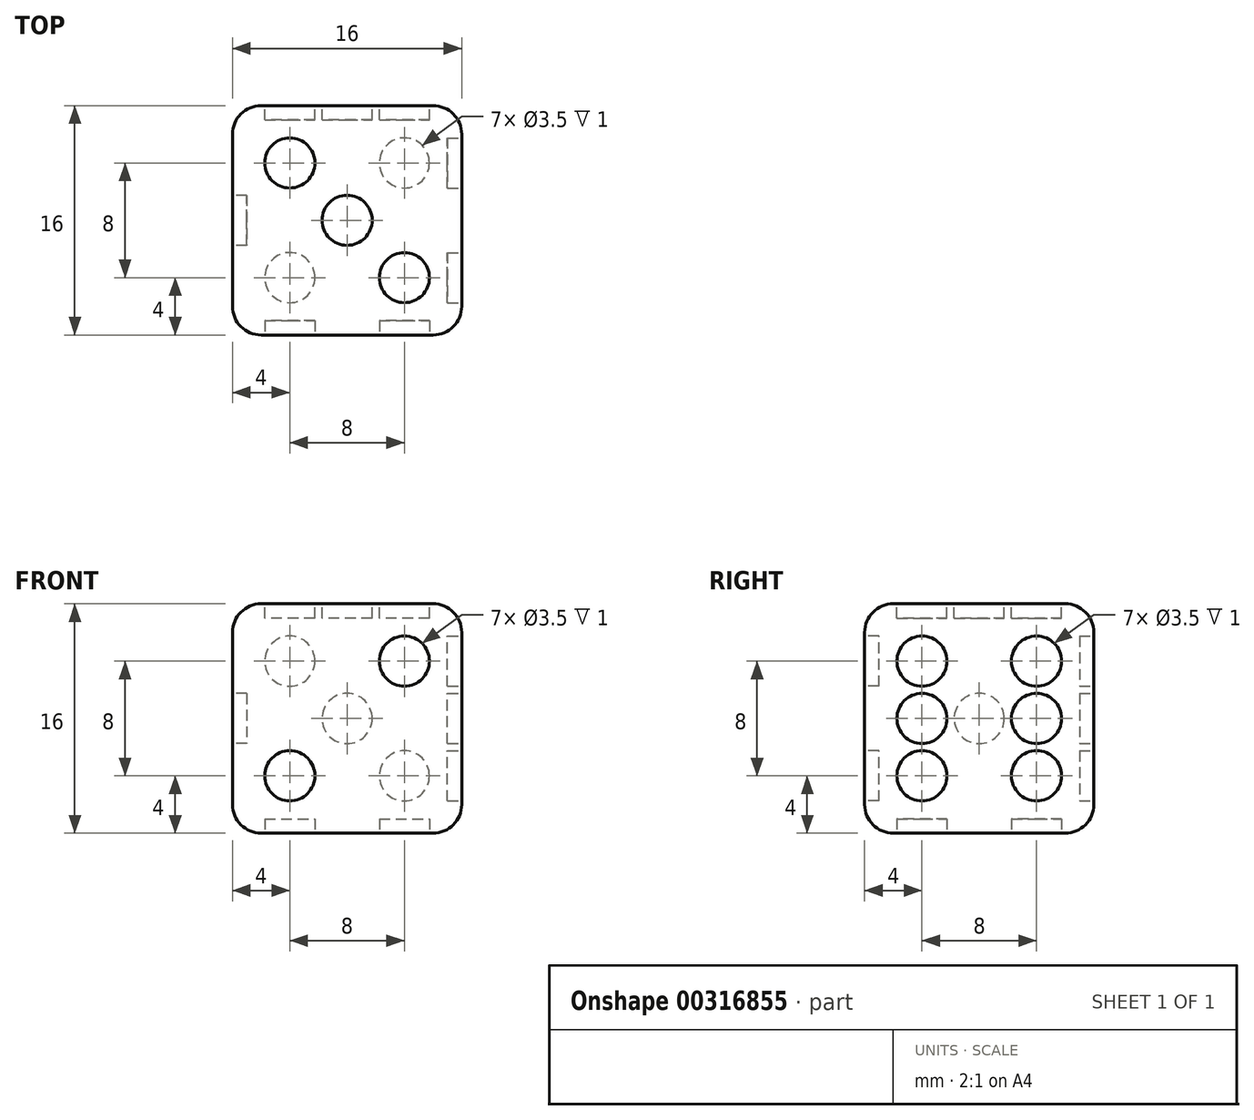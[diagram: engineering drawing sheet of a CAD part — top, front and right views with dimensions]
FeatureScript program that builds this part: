
annotation { "Feature Type Name" : "Feature", "Feature Type Description" : "" }
export const myFeature = defineFeature(function(context is Context, id is Id, definition is map)
    precondition{}
    {
        {
            var Q0;
            Q0=qCreatedBy(makeId("Top.planeOp"),FACE);
            var sketch = newSketch(context, id + "F0", { "sketchPlane" : qUnion([Q0])});
            skLineSegment(sketch, "E0.bottom", {"start": v(8, -8) * mm, "end": v(-8, -8) * mm});
            skLineSegment(sketch, "E0.top", {"start": v(8, 8) * mm, "end": v(-8, 8) * mm});
            skLineSegment(sketch, "E0.left", {"start": v(8, -8) * mm, "end": v(8, 8) * mm});
            skLineSegment(sketch, "E0.right", {"start": v(-8, -8) * mm, "end": v(-8, 8) * mm});
            skPoint(sketch, "E0.middle", {"position": v(0, 0) * mm});
            skSolve(sketch);
        }
        {
            var Q0;
            Q0=makeQuery(id+"F0.imprint","IMPRINT",FACE,{"disambiguationData":[TD([[makeQuery(id+"F0.imprint","IMPRINT",EDGE,{"derivedFrom":sQuery(id+"F0.wireOp",EDGE,"E0.bottom")}),-1.0]])]});
            extrude(context, id + "F1", {"entities" : qUnion([Q0]), "depth" : 16 * mm});
        }
        {
            var Q0;
            Q0=makeQuery(id+"F1.opExtrude","SWEPT_FACE",FACE,{"disambiguationData":[OSD([sQuery(id+"F0.wireOp",EDGE,"E0.top")])]});
            var sketch = newSketch(context, id + "F2", { "sketchPlane" : qUnion([Q0])});
            skCircle(sketch, "E1", {"center": v(-4, 4) * mm, "radius": 1.75 * mm});
            skCircle(sketch, "E2", {"center": v(4, 12) * mm, "radius": 1.75 * mm});
            skCircle(sketch, "E3", {"center": v(-4, 12) * mm, "radius": 1.75 * mm});
            skCircle(sketch, "E4", {"center": v(4, 4) * mm, "radius": 1.75 * mm});
            skCircle(sketch, "E5", {"center": v(0, 8) * mm, "radius": 1.75 * mm});
            skSolve(sketch);
        }
        {
            var Q0;
            Q0=makeQuery(id+"F2.imprint","IMPRINT",FACE,{"disambiguationData":[TD([[makeQuery(id+"F2.imprint","IMPRINT",EDGE,{"derivedFrom":sQuery(id+"F2.wireOp",EDGE,"E2")}),1.0]])]});
            var Q1;
            Q1=makeQuery(id+"F2.imprint","IMPRINT",FACE,{"disambiguationData":[TD([[makeQuery(id+"F2.imprint","IMPRINT",EDGE,{"derivedFrom":sQuery(id+"F2.wireOp",EDGE,"E1")}),1.0]])]});
            extrude(context, id + "F3", {"entities" : qUnion([Q0, Q1]), "operationType" : NewBodyOperationType.REMOVE, "oppositeDirection" : true, "depth" : 1 * mm});
        }
        {
            var Q0;
            Q0=makeQuery(id+"F2.imprint","IMPRINT",FACE,{"disambiguationData":[TD([[makeQuery(id+"F2.imprint","IMPRINT",EDGE,{"derivedFrom":sQuery(id+"F2.wireOp",EDGE,"E3")}),1.0]])]});
            var Q1;
            Q1=makeQuery(id+"F2.imprint","IMPRINT",FACE,{"disambiguationData":[TD([[makeQuery(id+"F2.imprint","IMPRINT",EDGE,{"derivedFrom":sQuery(id+"F2.wireOp",EDGE,"E5")}),1.0]])]});
            var Q2;
            Q2=makeQuery(id+"F2.imprint","IMPRINT",FACE,{"disambiguationData":[TD([[makeQuery(id+"F2.imprint","IMPRINT",EDGE,{"derivedFrom":sQuery(id+"F2.wireOp",EDGE,"E4")}),1.0]])]});
            extrude(context, id + "F4", {"entities" : qUnion([Q0, Q1, Q2]), "operationType" : NewBodyOperationType.REMOVE, "oppositeDirection" : true, "depth" : 1 * mm});
        }
        {
            var Q0;
            Q0=makeQuery(id+"F1.opExtrude","SWEPT_FACE",FACE,{"disambiguationData":[OSD([sQuery(id+"F0.wireOp",EDGE,"E0.bottom")])]});
            var sketch = newSketch(context, id + "F5", { "sketchPlane" : qUnion([Q0])});
            skCircle(sketch, "E6", {"center": v(-4, 4) * mm, "radius": 1.75 * mm});
            skCircle(sketch, "E7", {"center": v(4, 12) * mm, "radius": 1.75 * mm});
            skSolve(sketch);
        }
        {
            var Q0;
            Q0=makeQuery(id+"F5.imprint","IMPRINT",FACE,{"disambiguationData":[TD([[makeQuery(id+"F5.imprint","IMPRINT",EDGE,{"derivedFrom":sQuery(id+"F5.wireOp",EDGE,"E6")}),1.0]])]});
            var Q1;
            Q1=makeQuery(id+"F5.imprint","IMPRINT",FACE,{"disambiguationData":[TD([[makeQuery(id+"F5.imprint","IMPRINT",EDGE,{"derivedFrom":sQuery(id+"F5.wireOp",EDGE,"E7")}),1.0]])]});
            extrude(context, id + "F6", {"entities" : qUnion([Q0, Q1]), "operationType" : NewBodyOperationType.REMOVE, "oppositeDirection" : true, "depth" : 1 * mm});
        }
        {
            var Q0;
            Q0=makeQuery(id+"F1.opExtrude","CAP_FACE",FACE,{"disambiguationData":[OSD([sQuery(id+"F0.wireOp",EDGE,"E0.bottom"),sQuery(id+"F0.wireOp",EDGE,"E0.top"),sQuery(id+"F0.wireOp",EDGE,"E0.left"),sQuery(id+"F0.wireOp",EDGE,"E0.right")])],"isStart":false});
            var sketch = newSketch(context, id + "F7", { "sketchPlane" : qUnion([Q0])});
            skCircle(sketch, "E8", {"center": v(0, 0) * mm, "radius": 1.75 * mm});
            skCircle(sketch, "E9", {"center": v(4, -4) * mm, "radius": 1.75 * mm});
            skCircle(sketch, "E10", {"center": v(-4, 4) * mm, "radius": 1.75 * mm});
            skSolve(sketch);
        }
        {
            var Q0;
            Q0=makeQuery(id+"F7.imprint","IMPRINT",FACE,{"disambiguationData":[TD([[makeQuery(id+"F7.imprint","IMPRINT",EDGE,{"derivedFrom":sQuery(id+"F7.wireOp",EDGE,"h1jGjn2j-waux-BRHr-8ZsS-qUSvsllOvU67")}),1.0]])]});
            var Q1;
            Q1=makeQuery(id+"F7.imprint","IMPRINT",FACE,{"disambiguationData":[TD([[makeQuery(id+"F7.imprint","IMPRINT",EDGE,{"derivedFrom":sQuery(id+"F7.wireOp",EDGE,"E8")}),1.0]])]});
            var Q2;
            Q2=makeQuery(id+"F7.imprint","IMPRINT",FACE,{"disambiguationData":[TD([[makeQuery(id+"F7.imprint","IMPRINT",EDGE,{"derivedFrom":sQuery(id+"F7.wireOp",EDGE,"c6qNiyI0-zUlM-MVL6-RI8d-L9UIt0NrfZDj")}),1.0]])]});
            var Q3;
            Q3=makeQuery(id+"F7.imprint","IMPRINT",FACE,{"disambiguationData":[TD([[makeQuery(id+"F7.imprint","IMPRINT",EDGE,{"derivedFrom":sQuery(id+"F7.wireOp",EDGE,"E9")}),1.0]])]});
            var Q4;
            Q4=makeQuery(id+"F7.imprint","IMPRINT",FACE,{"disambiguationData":[TD([[makeQuery(id+"F7.imprint","IMPRINT",EDGE,{"derivedFrom":sQuery(id+"F7.wireOp",EDGE,"E10")}),1.0]])]});
            extrude(context, id + "F8", {"entities" : qUnion([Q0, Q1, Q2, Q3, Q4]), "operationType" : NewBodyOperationType.REMOVE, "oppositeDirection" : true, "depth" : 1 * mm});
        }
        {
            var Q0;
            Q0=makeQuery(id+"F1.opExtrude","SWEPT_FACE",FACE,{"disambiguationData":[OSD([sQuery(id+"F0.wireOp",EDGE,"E0.left")])]});
            var sketch = newSketch(context, id + "F9", { "sketchPlane" : qUnion([Q0])});
            skCircle(sketch, "E11", {"center": v(-4, 12) * mm, "radius": 1.75 * mm});
            skCircle(sketch, "E12", {"center": v(-4, 8) * mm, "radius": 1.75 * mm});
            skCircle(sketch, "E13", {"center": v(-4, 4) * mm, "radius": 1.75 * mm});
            skCircle(sketch, "E14", {"center": v(4, 4) * mm, "radius": 1.75 * mm});
            skCircle(sketch, "E15", {"center": v(4, 8) * mm, "radius": 1.75 * mm});
            skCircle(sketch, "E16", {"center": v(4, 12) * mm, "radius": 1.75 * mm});
            skSolve(sketch);
        }
        {
            var Q0;
            Q0=makeQuery(id+"F9.imprint","IMPRINT",FACE,{"disambiguationData":[TD([[makeQuery(id+"F9.imprint","IMPRINT",EDGE,{"derivedFrom":sQuery(id+"F9.wireOp",EDGE,"E11")}),1.0]])]});
            var Q1;
            Q1=makeQuery(id+"F9.imprint","IMPRINT",FACE,{"disambiguationData":[TD([[makeQuery(id+"F9.imprint","IMPRINT",EDGE,{"derivedFrom":sQuery(id+"F9.wireOp",EDGE,"E13")}),1.0]])]});
            var Q2;
            Q2=makeQuery(id+"F9.imprint","IMPRINT",FACE,{"disambiguationData":[TD([[makeQuery(id+"F9.imprint","IMPRINT",EDGE,{"derivedFrom":sQuery(id+"F9.wireOp",EDGE,"E14")}),1.0]])]});
            var Q3;
            Q3=makeQuery(id+"F9.imprint","IMPRINT",FACE,{"disambiguationData":[TD([[makeQuery(id+"F9.imprint","IMPRINT",EDGE,{"derivedFrom":sQuery(id+"F9.wireOp",EDGE,"E15")}),1.0]])]});
            var Q4;
            Q4=makeQuery(id+"F9.imprint","IMPRINT",FACE,{"disambiguationData":[TD([[makeQuery(id+"F9.imprint","IMPRINT",EDGE,{"derivedFrom":sQuery(id+"F9.wireOp",EDGE,"E16")}),1.0]])]});
            var Q5;
            Q5=makeQuery(id+"F9.imprint","IMPRINT",FACE,{"disambiguationData":[TD([[makeQuery(id+"F9.imprint","IMPRINT",EDGE,{"derivedFrom":sQuery(id+"F9.wireOp",EDGE,"E12")}),1.0]])]});
            extrude(context, id + "F10", {"entities" : qUnion([Q0, Q1, Q2, Q3, Q4, Q5]), "operationType" : NewBodyOperationType.REMOVE, "oppositeDirection" : true, "depth" : 1 * mm});
        }
        {
            var Q0;
            Q0=makeQuery(id+"F1.opExtrude","CAP_FACE",FACE,{"disambiguationData":[OSD([sQuery(id+"F0.wireOp",EDGE,"E0.bottom"),sQuery(id+"F0.wireOp",EDGE,"E0.top"),sQuery(id+"F0.wireOp",EDGE,"E0.left"),sQuery(id+"F0.wireOp",EDGE,"E0.right")])],"isStart":true});
            var sketch = newSketch(context, id + "F11", { "sketchPlane" : qUnion([Q0])});
            skCircle(sketch, "E17", {"center": v(4, -4) * mm, "radius": 1.75 * mm});
            skCircle(sketch, "E18", {"center": v(-4, -4) * mm, "radius": 1.75 * mm});
            skCircle(sketch, "E19", {"center": v(-4, 4) * mm, "radius": 1.75 * mm});
            skCircle(sketch, "E20", {"center": v(4, 4) * mm, "radius": 1.75 * mm});
            skSolve(sketch);
        }
        {
            var Q0;
            Q0=makeQuery(id+"F11.imprint","IMPRINT",FACE,{"disambiguationData":[TD([[makeQuery(id+"F11.imprint","IMPRINT",EDGE,{"derivedFrom":sQuery(id+"F11.wireOp",EDGE,"E17")}),1.0]])]});
            var Q1;
            Q1=makeQuery(id+"F11.imprint","IMPRINT",FACE,{"disambiguationData":[TD([[makeQuery(id+"F11.imprint","IMPRINT",EDGE,{"derivedFrom":sQuery(id+"F11.wireOp",EDGE,"E19")}),1.0]])]});
            var Q2;
            Q2=makeQuery(id+"F11.imprint","IMPRINT",FACE,{"disambiguationData":[TD([[makeQuery(id+"F11.imprint","IMPRINT",EDGE,{"derivedFrom":sQuery(id+"F11.wireOp",EDGE,"E20")}),1.0]])]});
            var Q3;
            Q3=makeQuery(id+"F11.imprint","IMPRINT",FACE,{"disambiguationData":[TD([[makeQuery(id+"F11.imprint","IMPRINT",EDGE,{"derivedFrom":sQuery(id+"F11.wireOp",EDGE,"E18")}),1.0]])]});
            extrude(context, id + "F12", {"entities" : qUnion([Q0, Q1, Q2, Q3]), "operationType" : NewBodyOperationType.REMOVE, "oppositeDirection" : true, "depth" : 1 * mm});
        }
        {
            var Q0;
            Q0=makeQuery(id+"F1.opExtrude","SWEPT_FACE",FACE,{"disambiguationData":[OSD([sQuery(id+"F0.wireOp",EDGE,"E0.right")])]});
            var sketch = newSketch(context, id + "F13", { "sketchPlane" : qUnion([Q0])});
            skCircle(sketch, "E21", {"center": v(0, 8) * mm, "radius": 1.75 * mm});
            skSolve(sketch);
        }
        {
            var Q0;
            Q0=makeQuery(id+"F13.imprint","IMPRINT",FACE,{"disambiguationData":[TD([[makeQuery(id+"F13.imprint","IMPRINT",EDGE,{"derivedFrom":sQuery(id+"F13.wireOp",EDGE,"E21")}),1.0]])]});
            extrude(context, id + "F14", {"entities" : qUnion([Q0]), "operationType" : NewBodyOperationType.REMOVE, "oppositeDirection" : true, "depth" : 1 * mm});
        }
        {
            var Q0;
            Q0=makeQuery(id+"F1.opExtrude","CAP_EDGE",EDGE,{"disambiguationData":[OSD([sQuery(id+"F0.wireOp",EDGE,"E0.left")])],"isStart":false});
            var Q1;
            Q1=makeQuery(id+"F1.opExtrude","CAP_EDGE",EDGE,{"disambiguationData":[OSD([sQuery(id+"F0.wireOp",EDGE,"E0.top")])],"isStart":false});
            var Q2;
            Q2=makeQuery(id+"F1.opExtrude","CAP_EDGE",EDGE,{"disambiguationData":[OSD([sQuery(id+"F0.wireOp",EDGE,"E0.right")])],"isStart":false});
            var Q3;
            Q3=makeQuery(id+"F1.opExtrude","CAP_EDGE",EDGE,{"disambiguationData":[OSD([sQuery(id+"F0.wireOp",EDGE,"E0.bottom")])],"isStart":false});
            var Q4;
            Q4=makeQuery(id+"F1.opExtrude","SWEPT_EDGE",EDGE,{"disambiguationData":[OSD([sQuery(id+"F0.wireOp",EDGE,"E0.bottom"),sQuery(id+"F0.wireOp",EDGE,"E0.right")])]});
            var Q5;
            Q5=makeQuery(id+"F1.opExtrude","SWEPT_EDGE",EDGE,{"disambiguationData":[OSD([sQuery(id+"F0.wireOp",EDGE,"E0.top"),sQuery(id+"F0.wireOp",EDGE,"E0.right")])]});
            var Q6;
            Q6=makeQuery(id+"F1.opExtrude","CAP_EDGE",EDGE,{"disambiguationData":[OSD([sQuery(id+"F0.wireOp",EDGE,"E0.right")])],"isStart":true});
            var Q7;
            Q7=makeQuery(id+"F1.opExtrude","CAP_EDGE",EDGE,{"disambiguationData":[OSD([sQuery(id+"F0.wireOp",EDGE,"E0.bottom")])],"isStart":true});
            var Q8;
            Q8=makeQuery(id+"F1.opExtrude","SWEPT_EDGE",EDGE,{"disambiguationData":[OSD([sQuery(id+"F0.wireOp",EDGE,"E0.bottom"),sQuery(id+"F0.wireOp",EDGE,"E0.left")])]});
            var Q9;
            Q9=makeQuery(id+"F1.opExtrude","CAP_EDGE",EDGE,{"disambiguationData":[OSD([sQuery(id+"F0.wireOp",EDGE,"E0.left")])],"isStart":true});
            var Q10;
            Q10=makeQuery(id+"F1.opExtrude","SWEPT_EDGE",EDGE,{"disambiguationData":[OSD([sQuery(id+"F0.wireOp",EDGE,"E0.top"),sQuery(id+"F0.wireOp",EDGE,"E0.left")])]});
            var Q11;
            Q11=makeQuery(id+"F1.opExtrude","CAP_EDGE",EDGE,{"disambiguationData":[OSD([sQuery(id+"F0.wireOp",EDGE,"E0.top")])],"isStart":true});
            fillet(context, id + "F15", {"entities" : qUnion([Q0, Q1, Q2, Q3, Q4, Q5, Q6, Q7, Q8, Q9, Q10, Q11]), "radius" : 2 * mm, "tangentPropagation" : true, "allowEdgeOverflow" : false});
        }
    });
